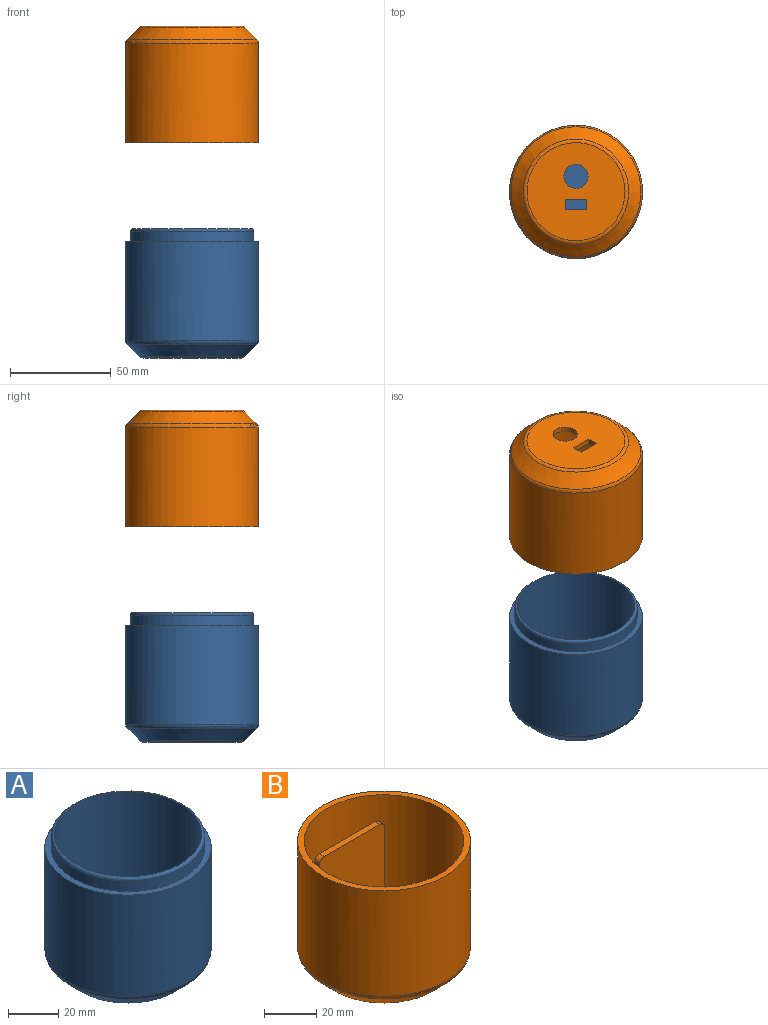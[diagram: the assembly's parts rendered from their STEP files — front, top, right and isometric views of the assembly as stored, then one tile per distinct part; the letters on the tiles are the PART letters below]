
ASSEMBLY  parts=2 mates=1
PART A: 11 faces, bbox 71.5x71.5x64.4 mm
  f0: cylinder r=33.04mm len=66.08mm, axis (0,0,-1), area 10240.3mm2, adj f1,f5
  f1: plane 66.08x66.08mm, normal (0,0,1), area 507mm2, adj f0,f6
  f2: plane 48.74x48.74mm, normal (0,0,-1), area 1865.5mm2, adj f4
  f3: cone r=33.04mm half-angle=45deg, axis (0,0,1), area 1592.7mm2, adj f4,f5
  f4: torus R=24.37mm, axis (0,0,1), area 317.3mm2, adj f2,f3
  f5: torus R=30.5mm, axis (0,0,-1), area 411mm2, adj f0,f3
  f6: cylinder r=30.5mm len=61mm, axis (0,0,-1), area 973.5mm2, adj f1,f10
  f7: plane 47.68x47.68mm, normal (0,0,1), area 1785.8mm2, adj f8
  f8: cone r=30.35mm half-angle=45deg, axis (0,0,1), area 1270.5mm2, adj f7,f9
  f9: cylinder r=29.23mm len=58.46mm, axis (0,0,-1), area 10129.1mm2, adj f8,f10
  f10: torus R=29.23mm, axis (0,0,1), area 376.5mm2, adj f6,f9
PART B: 22 faces, bbox 71.7x71.7x58.2 mm
  f0: plane 28.27x4.52mm, normal (0,0,1), area 86.9mm2, adj f1,f18
  f1: cone r=31.24mm half-angle=45deg, axis (0,0,1), area 1481.5mm2, adj f0,f2,f7,f15,f16,f17,f18
  f2: plane 48.74x41.68mm, normal (0,0,1), area 1532.6mm2, adj f1,f10,f11,f12,f13,f14,f16
  f3: cylinder r=33.04mm len=66.08mm, axis (0,0,-1), area 10240.3mm2, adj f4,f9
  f4: plane 66.08x66.08mm, normal (0,0,1), area 507mm2, adj f3,f7
  f5: plane 48.74x48.74mm, normal (0,0,-1), area 1699.4mm2, adj f8,f10,f11,f12,f13,f14
  f6: cone r=33.04mm half-angle=45deg, axis (0,0,1), area 1592.7mm2, adj f8,f9
  f7: cylinder r=30.5mm len=61mm, axis (0,0,-1), area 9453.1mm2, adj f1,f4
  f8: torus R=24.37mm, axis (0,0,1), area 317.3mm2, adj f5,f6
  f9: torus R=30.5mm, axis (0,0,-1), area 411mm2, adj f3,f6
  f10: plane 10.6x2.54mm, normal (0,-1,0), area 26.9mm2, adj f2,f5,f11,f12
  f11: plane 5x2.54mm, normal (-1,0,0), area 12.7mm2, adj f2,f5,f10,f13
  f12: plane 5x2.54mm, normal (1,0,0), area 12.7mm2, adj f2,f5,f10,f13
  f13: plane 10.6x2.54mm, normal (0,1,0), area 26.9mm2, adj f2,f5,f11,f12
  f14: cylinder r=6mm len=12mm, axis (0,0,-1), area 95.8mm2, adj f2,f5
  f15: plane 44.29x2.62mm, normal (-1,0,0), area 110mm2, adj f1,f16,f18,f20
  f16: plane 47x35mm, normal (0,-1,0), area 1642.1mm2, adj f1,f2,f15,f17,f19,f20,f21
  f17: plane 44.29x2.62mm, normal (1,0,0), area 110mm2, adj f1,f16,f18,f21
  f18: plane 47.15x35.15mm, normal (0,1,0), area 1635.3mm2, adj f0,f1,f15,f17,f19,f20,f21
  f19: plane 29.92x2.54mm, normal (0,0,1), area 76mm2, adj f16,f18,f20,f21
  f20: cylinder r=2.54mm len=2.54mm, axis (0,1,0), area 10.1mm2, adj f15,f16,f18,f19
  f21: cylinder r=2.54mm len=2.54mm, axis (0,-1,0), area 10.1mm2, adj f16,f17,f18,f19
PLACE A t=(-4.96,6.79,-55.09)mm
PLACE B rot(axis=(1,0,0),180deg) t=(-4.96,6.79,109.94)mm
MATE cylindrical B.f1 <-> A.f0  axis (0,0,1) through (-4.96,6.79,76.6)mm
